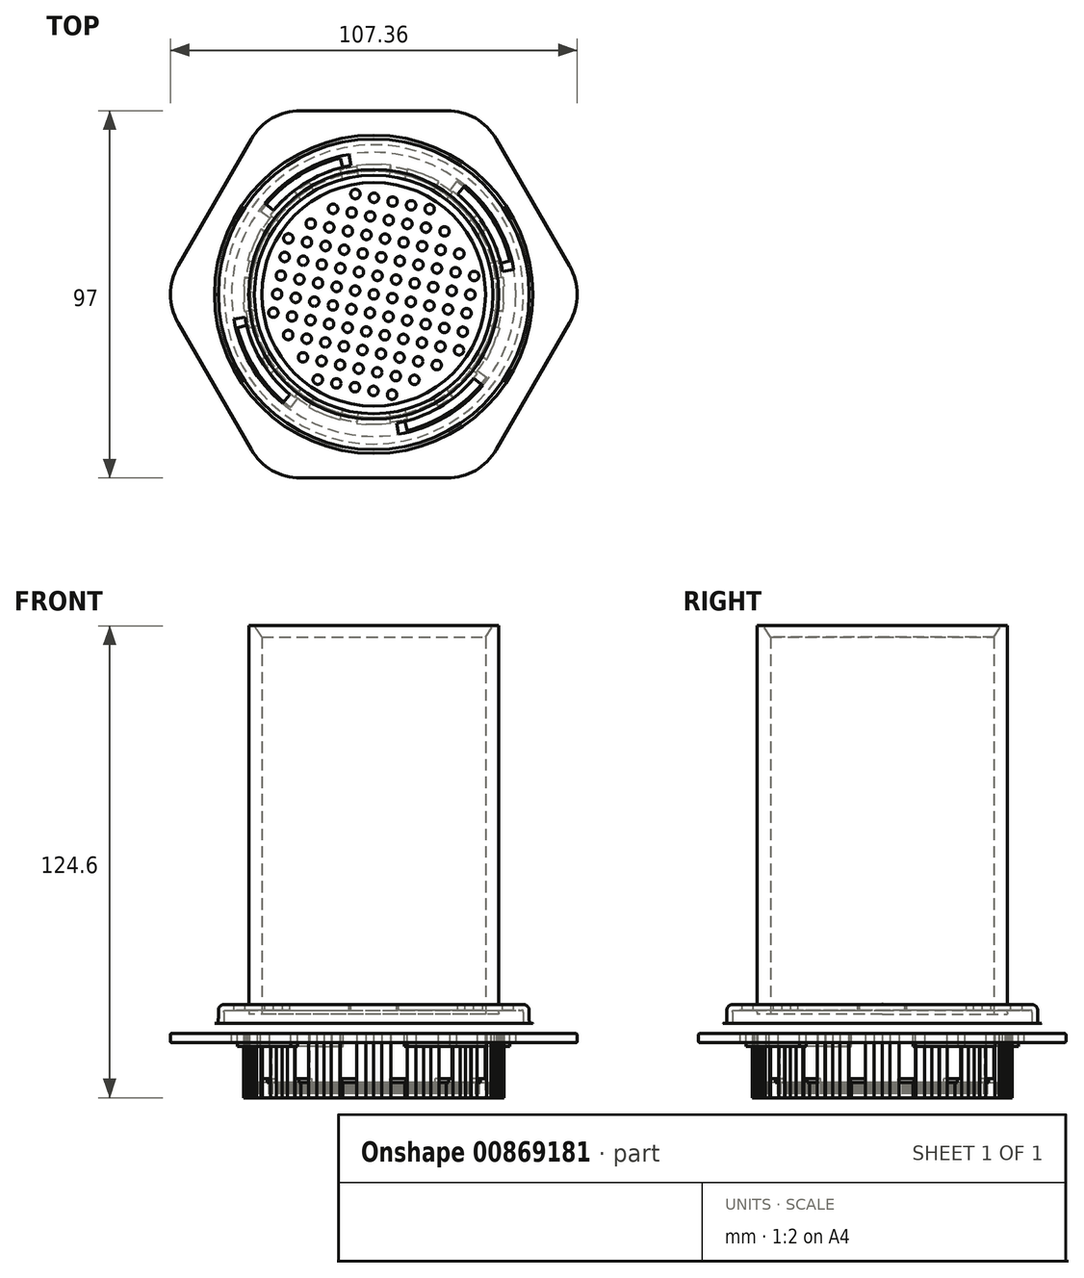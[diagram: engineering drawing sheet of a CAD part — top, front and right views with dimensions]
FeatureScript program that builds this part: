
annotation { "Feature Type Name" : "Feature", "Feature Type Description" : "" }
export const myFeature = defineFeature(function(context is Context, id is Id, definition is map)
    precondition{}
    {
        {
            var Q0;
            Q0=qCreatedBy(makeId("Top.planeOp"),FACE);
            var sketch = newSketch(context, id + "F0", { "sketchPlane" : qUnion([Q0])});
            skCircle(sketch, "E0.cCircle", {"center": v(0, 0) * mm, "radius": 48.5 * mm, "construction": true});
            skLineSegment(sketch, "E0.0", {"start": v(28, -48.5) * mm, "end": v(-28, -48.5) * mm});
            skLineSegment(sketch, "E0.1", {"start": v(-28, -48.5) * mm, "end": v(-56, 0) * mm});
            skLineSegment(sketch, "E0.2", {"start": v(-56, 0) * mm, "end": v(-28, 48.5) * mm});
            skLineSegment(sketch, "E0.3", {"start": v(-28, 48.5) * mm, "end": v(28, 48.5) * mm});
            skLineSegment(sketch, "E0.4", {"start": v(28, 48.5) * mm, "end": v(56, 0) * mm});
            skLineSegment(sketch, "E0.5", {"start": v(56, 0) * mm, "end": v(28, -48.5) * mm});
            skPoint(sketch, "E0.0.midPoint", {"position": v(0, -48.5) * mm});
            skCircle(sketch, "E1", {"center": v(0, 0) * mm, "radius": 42 * mm, "construction": true});
            skSolve(sketch);
        }
        {
            var Q0;
            Q0=makeQuery(id+"F0.imprint","IMPRINT",FACE,{"disambiguationData":[TD([[makeQuery(id+"F0.imprint","IMPRINT",EDGE,{"derivedFrom":sQuery(id+"F0.wireOp",EDGE,"E0.0")}),-1.0]])]});
            extrude(context, id + "F1", {"entities" : qUnion([Q0]), "oppositeDirection" : true, "depth" : 2.5 * mm, "offsetDistance" : 25 * mm});
        }
        {
            var Q0;
            Q0=makeQuery(id+"F1.opExtrude","CAP_EDGE",EDGE,{"disambiguationData":[OSD([sQuery(id+"F0.wireOp",EDGE,"E0.0")])],"isStart":false});
            var Q1;
            Q1=makeQuery(id+"F1.opExtrude","CAP_EDGE",EDGE,{"disambiguationData":[OSD([sQuery(id+"F0.wireOp",EDGE,"E0.5")])],"isStart":false});
            var Q2;
            Q2=makeQuery(id+"F1.opExtrude","CAP_EDGE",EDGE,{"disambiguationData":[OSD([sQuery(id+"F0.wireOp",EDGE,"E0.4")])],"isStart":false});
            var Q3;
            Q3=makeQuery(id+"F1.opExtrude","CAP_EDGE",EDGE,{"disambiguationData":[OSD([sQuery(id+"F0.wireOp",EDGE,"E0.3")])],"isStart":false});
            var Q4;
            Q4=makeQuery(id+"F1.opExtrude","CAP_EDGE",EDGE,{"disambiguationData":[OSD([sQuery(id+"F0.wireOp",EDGE,"E0.2")])],"isStart":false});
            var Q5;
            Q5=makeQuery(id+"F1.opExtrude","CAP_EDGE",EDGE,{"disambiguationData":[OSD([sQuery(id+"F0.wireOp",EDGE,"E0.1")])],"isStart":false});
            var Q6;
            Q6=makeQuery(id+"F1.opExtrude","CAP_FACE",FACE,{"disambiguationData":[OSD([sQuery(id+"F0.wireOp",EDGE,"E0.0"),sQuery(id+"F0.wireOp",EDGE,"E0.1"),sQuery(id+"F0.wireOp",EDGE,"E0.2"),sQuery(id+"F0.wireOp",EDGE,"E0.3"),sQuery(id+"F0.wireOp",EDGE,"E0.4"),sQuery(id+"F0.wireOp",EDGE,"E0.5")])],"isStart":true});
            fillet(context, id + "F2", {"entities" : qUnion([Q0, Q1, Q2, Q3, Q4, Q5, Q6]), "radius" : .5 * mm, "tangentPropagation" : true, "allowEdgeOverflow" : false});
        }
        {
            var Q0;
            Q0=makeQuery(id+"F1.opExtrude","SWEPT_EDGE",EDGE,{"disambiguationData":[OSD([sQuery(id+"F0.wireOp",EDGE,"E0.0"),sQuery(id+"F0.wireOp",EDGE,"E0.1")])]});
            var Q1;
            Q1=makeQuery(id+"F1.opExtrude","SWEPT_EDGE",EDGE,{"disambiguationData":[OSD([sQuery(id+"F0.wireOp",EDGE,"E0.0"),sQuery(id+"F0.wireOp",EDGE,"E0.5")])]});
            var Q2;
            Q2=makeQuery(id+"F1.opExtrude","SWEPT_EDGE",EDGE,{"disambiguationData":[OSD([sQuery(id+"F0.wireOp",EDGE,"E0.4"),sQuery(id+"F0.wireOp",EDGE,"E0.5")])]});
            var Q3;
            Q3=makeQuery(id+"F1.opExtrude","SWEPT_EDGE",EDGE,{"disambiguationData":[OSD([sQuery(id+"F0.wireOp",EDGE,"E0.3"),sQuery(id+"F0.wireOp",EDGE,"E0.4")])]});
            var Q4;
            Q4=makeQuery(id+"F1.opExtrude","SWEPT_EDGE",EDGE,{"disambiguationData":[OSD([sQuery(id+"F0.wireOp",EDGE,"E0.2"),sQuery(id+"F0.wireOp",EDGE,"E0.3")])]});
            var Q5;
            Q5=makeQuery(id+"F1.opExtrude","SWEPT_EDGE",EDGE,{"disambiguationData":[OSD([sQuery(id+"F0.wireOp",EDGE,"E0.1"),sQuery(id+"F0.wireOp",EDGE,"E0.2")])]});
            fillet(context, id + "F3", {"entities" : qUnion([Q0, Q1, Q2, Q3, Q4, Q5]), "radius" : 15 * mm, "tangentPropagation" : true, "allowEdgeOverflow" : false});
        }
        {
            var Q0;
            Q0=qCreatedBy(makeId("Right.planeOp"),FACE);
            var sketch = newSketch(context, id + "F4", { "sketchPlane" : qUnion([Q0])});
            skLineSegment(sketch, "E2", {"start": v(-39.5, 2.6) * mm, "end": v(-41, 2.6) * mm, "construction": true});
            skLineSegment(sketch, "E3", {"start": v(-39.5, 2.6) * mm, "end": v(-41, 2.6) * mm});
            skLineSegment(sketch, "E4", {"start": v(-41, 5.1) * mm, "end": v(-41, 7.6) * mm});
            skLineSegment(sketch, "E5", {"start": v(-41, 7.6) * mm, "end": v(-33.5, 7.6) * mm});
            skLineSegment(sketch, "E6", {"start": v(-33, 8.1) * mm, "end": v(-33, 107.6) * mm});
            skLineSegment(sketch, "E7", {"start": v(-33, 107.6) * mm, "end": v(-31.5, 107.6) * mm});
            skLineSegment(sketch, "E8", {"start": v(-29.5, 104.6) * mm, "end": v(-31.5, 107.6) * mm});
            skLineSegment(sketch, "E9", {"start": v(0, 0) * mm, "end": v(0, 27.78) * mm, "construction": true});
            skLineSegment(sketch, "E10", {"start": v(-41, 2.6) * mm, "end": v(-42, 2.6) * mm});
            skFitSpline(sketch, "E11", {"points": [v(-42, 2.6) * mm, v(-41, 5.1) * mm], "startDerivative": vector(3, 0) * mm, "endDerivative": vector(0, 7.5) * mm});
            skLineSegment(sketch, "E12", {"start": v(-29.5, -6.9) * mm, "end": v(-31, -6.9) * mm});
            skLineSegment(sketch, "E13", {"start": v(-31, -6.9) * mm, "end": v(-33, -3.9) * mm});
            skLineSegment(sketch, "E14", {"start": v(-29.5, 104.6) * mm, "end": v(-29.5, -6.9) * mm});
            skLineSegment(sketch, "E15", {"start": v(-33.5, 6.1) * mm, "end": v(-39, 6.1) * mm});
            skLineSegment(sketch, "E16", {"start": v(-39.5, 5.6) * mm, "end": v(-39.5, 2.6) * mm});
            skPoint(sketch, "E17.end.orphan", {"position": v(-33, 2.6) * mm});
            skLineSegment(sketch, "E18", {"start": v(-33, 5.6) * mm, "end": v(-33, -3.9) * mm});
            skFitSpline(sketch, "E19", {"points": [v(-33.5, 6.1) * mm, v(-33, 5.6) * mm], "startDerivative": vector(1.5, 0) * mm, "endDerivative": vector(0, -1.5) * mm});
            skFitSpline(sketch, "E20", {"points": [v(-39.5, 5.6) * mm, v(-39, 6.1) * mm], "startDerivative": vector(0, 1.5) * mm, "endDerivative": vector(1.5, 0) * mm});
            skFitSpline(sketch, "E21", {"points": [v(-33, 8.1) * mm, v(-33.5, 7.6) * mm], "startDerivative": vector(0, -1.5) * mm, "endDerivative": vector(-1.5, 0) * mm});
            skSolve(sketch);
        }
        {
            var Q0;
            Q0=makeQuery(id+"F4.imprint","IMPRINT",FACE,{"disambiguationData":[TD([[makeQuery(id+"F4.imprint","IMPRINT",EDGE,{"derivedFrom":sQuery(id+"F4.wireOp",EDGE,"E3")}),-1.0]])]});
            var Q1;
            Q1=sQuery(id+"F4.wireOp",EDGE,"E9");
            revolve(context, id + "F5", {"surfaceOperationType" : NewSurfaceOperationType.NEW, "entities" : qUnion([Q0]), "axis" : qUnion([Q1]), "revolveType" : RevolveType.FULL});
        }
        {
            var Q0;
            Q0=makeQuery(id+"F5.opRevolve","SWEPT_EDGE",EDGE,{"disambiguationData":[OSD([sQuery(id+"F4.wireOp",EDGE,"E4"),sQuery(id+"F4.wireOp",EDGE,"E5")])]});
            fillet(context, id + "F6", {"entities" : qUnion([Q0]), "radius" : 1.5 * mm, "tangentPropagation" : true, "allowEdgeOverflow" : false});
        }
        {
            var Q0;
            Q0=makeQuery(id+"F1.opExtrude","CAP_FACE",FACE,{"disambiguationData":[OSD([sQuery(id+"F0.wireOp",EDGE,"E0.0"),sQuery(id+"F0.wireOp",EDGE,"E0.1"),sQuery(id+"F0.wireOp",EDGE,"E0.2"),sQuery(id+"F0.wireOp",EDGE,"E0.3"),sQuery(id+"F0.wireOp",EDGE,"E0.4"),sQuery(id+"F0.wireOp",EDGE,"E0.5")])],"isStart":true});
            var sketch = newSketch(context, id + "F7", { "sketchPlane" : qUnion([Q0])});
            skArc(sketch, "E22", {"start": v(-6.51, 36.93) * mm, "mid": v(9.7, 36.22) * mm, "end": v(24.1, 28.73) * mm});
            skLineSegment(sketch, "E23", {"start": v(-6, 33.98) * mm, "end": v(-6.51, 36.93) * mm});
            skLineSegment(sketch, "E24", {"start": v(24.1, 28.73) * mm, "end": v(22.18, 26.43) * mm});
            skArc(sketch, "E25", {"start": v(22.18, 26.43) * mm, "mid": v(29.88, 17.25) * mm, "end": v(33.98, 6) * mm});
            skArc(sketch, "E26", {"start": v(36.93, 6.51) * mm, "mid": v(36.22, -9.7) * mm, "end": v(28.73, -24.1) * mm});
            skLineSegment(sketch, "E27", {"start": v(33.98, 6) * mm, "end": v(36.93, 6.51) * mm});
            skLineSegment(sketch, "E28", {"start": v(28.73, -24.1) * mm, "end": v(26.43, -22.18) * mm});
            skArc(sketch, "E29", {"start": v(26.43, -22.18) * mm, "mid": v(17.25, -29.88) * mm, "end": v(6, -33.98) * mm});
            skArc(sketch, "E30", {"start": v(6.51, -36.93) * mm, "mid": v(-9.7, -36.22) * mm, "end": v(-24.1, -28.73) * mm});
            skLineSegment(sketch, "E31", {"start": v(6, -33.98) * mm, "end": v(6.51, -36.93) * mm});
            skLineSegment(sketch, "E32", {"start": v(-24.1, -28.73) * mm, "end": v(-22.18, -26.43) * mm});
            skArc(sketch, "E33", {"start": v(-22.18, -26.43) * mm, "mid": v(-29.88, -17.25) * mm, "end": v(-33.98, -6) * mm});
            skArc(sketch, "E34", {"start": v(-36.93, -6.51) * mm, "mid": v(-36.22, 9.7) * mm, "end": v(-28.73, 24.1) * mm});
            skLineSegment(sketch, "E35", {"start": v(-33.98, -6) * mm, "end": v(-36.93, -6.51) * mm});
            skLineSegment(sketch, "E36", {"start": v(-28.73, 24.1) * mm, "end": v(-26.43, 22.18) * mm});
            skArc(sketch, "E37", {"start": v(-26.43, 22.18) * mm, "mid": v(-17.25, 29.88) * mm, "end": v(-6, 33.98) * mm});
            skLineSegment(sketch, "E38.0", {"start": v(-33.98, -6) * mm, "end": v(0, 0) * mm, "construction": true});
            skLineSegment(sketch, "E39.0", {"start": v(0, 0) * mm, "end": v(33.98, 6) * mm, "construction": true});
            skLineSegment(sketch, "E40.0", {"start": v(6.51, -36.93) * mm, "end": v(0, 0) * mm, "construction": true});
            skLineSegment(sketch, "E41.0", {"start": v(0, 0) * mm, "end": v(-6.51, 36.93) * mm, "construction": true});
            skSolve(sketch);
        }
        {
            var Q0;
            Q0 = qSketchRegion(id + "F7", true);
            extrude(context, id + "F8", {"entities" : qUnion([Q0]), "operationType" : NewBodyOperationType.REMOVE, "oppositeDirection" : true, "depth" : 10 * mm, "offsetDistance" : 25 * mm, "symmetric" : true});
        }
        {
            var Q0;
            Q0=makeQuery(id+"F5.opRevolve","SWEPT_FACE",FACE,{"disambiguationData":[OSD([sQuery(id+"F4.wireOp",EDGE,"E5")])]});
            var sketch = newSketch(context, id + "F9", { "sketchPlane" : qUnion([Q0])});
            skLineSegment(sketch, "E42", {"start": v(22.18, 26.43) * mm, "end": v(24.1, 28.73) * mm});
            skLineSegment(sketch, "E43.3.2", {"start": v(33.98, 6) * mm, "end": v(36.93, 6.51) * mm});
            skPoint(sketch, "E43.center", {"position": v(0, 0) * mm});
            skArc(sketch, "E44", {"start": v(24.1, 28.73) * mm, "mid": v(32.48, 18.75) * mm, "end": v(36.93, 6.51) * mm});
            skArc(sketch, "E45", {"start": v(22.18, 26.43) * mm, "mid": v(29.88, 17.25) * mm, "end": v(33.98, 6) * mm});
            skArc(sketch, "E46.1.0", {"start": v(-28.73, 24.1) * mm, "mid": v(-18.75, 32.48) * mm, "end": v(-6.51, 36.93) * mm});
            skLineSegment(sketch, "E46.1.1", {"start": v(-6, 33.98) * mm, "end": v(-6.51, 36.93) * mm});
            skLineSegment(sketch, "E46.1.2", {"start": v(-26.43, 22.18) * mm, "end": v(-28.73, 24.1) * mm});
            skArc(sketch, "E46.1.3", {"start": v(-26.43, 22.18) * mm, "mid": v(-17.25, 29.88) * mm, "end": v(-6, 33.98) * mm});
            skArc(sketch, "E46.2.0", {"start": v(-24.1, -28.73) * mm, "mid": v(-32.48, -18.75) * mm, "end": v(-36.93, -6.51) * mm});
            skLineSegment(sketch, "E46.2.1", {"start": v(-33.98, -6) * mm, "end": v(-36.93, -6.51) * mm});
            skLineSegment(sketch, "E46.2.2", {"start": v(-22.18, -26.43) * mm, "end": v(-24.1, -28.73) * mm});
            skArc(sketch, "E46.2.3", {"start": v(-22.18, -26.43) * mm, "mid": v(-29.88, -17.25) * mm, "end": v(-33.98, -6) * mm});
            skArc(sketch, "E46.3.0", {"start": v(28.73, -24.1) * mm, "mid": v(18.75, -32.48) * mm, "end": v(6.51, -36.93) * mm});
            skLineSegment(sketch, "E46.3.1", {"start": v(6, -33.98) * mm, "end": v(6.51, -36.93) * mm});
            skLineSegment(sketch, "E46.3.2", {"start": v(26.43, -22.18) * mm, "end": v(28.73, -24.1) * mm});
            skArc(sketch, "E46.3.3", {"start": v(26.43, -22.18) * mm, "mid": v(17.25, -29.88) * mm, "end": v(6, -33.98) * mm});
            skSolve(sketch);
        }
        {
            var Q0;
            Q0 = qSketchRegion(id + "F9", true);
            extrude(context, id + "F10", {"entities" : qUnion([Q0]), "operationType" : NewBodyOperationType.REMOVE, "oppositeDirection" : true, "depth" : 10 * mm, "offsetDistance" : 25 * mm});
        }
        {
            var Q0;
            Q0=qCreatedBy(makeId("Top.planeOp"),FACE);
            var sketch = newSketch(context, id + "F11", { "sketchPlane" : qUnion([Q0])});
            skCircle(sketch, "E47", {"center": v(0, 0) * mm, "radius": 34 * mm});
            skSolve(sketch);
        }
        {
            var Q0;
            Q0 = qSketchRegion(id + "F11", true);
            extrude(context, id + "F12", {"entities" : qUnion([Q0]), "oppositeDirection" : true, "depth" : 17 * mm, "offsetDistance" : 25 * mm});
        }
        {
            var Q0;
            Q0=makeQuery(id+"F12.opExtrude","CAP_FACE",FACE,{"disambiguationData":[OSD([sQuery(id+"F11.wireOp",EDGE,"E47")])],"isStart":true});
            var sketch = newSketch(context, id + "F13", { "sketchPlane" : qUnion([Q0])});
            skCircle(sketch, "E48", {"center": v(0, 0) * mm, "radius": 32.5 * mm});
            skSolve(sketch);
        }
        {
            var Q0;
            Q0 = qSketchRegion(id + "F13", true);
            extrude(context, id + "F14", {"entities" : qUnion([Q0]), "operationType" : NewBodyOperationType.REMOVE, "oppositeDirection" : true, "depth" : 13 * mm, "offsetDistance" : 25 * mm});
        }
        {
            var Q0;
            Q0=makeQuery(id+"F12.opExtrude","CAP_FACE",FACE,{"disambiguationData":[OSD([sQuery(id+"F11.wireOp",EDGE,"E47")])],"isStart":true});
            var sketch = newSketch(context, id + "F15", { "sketchPlane" : qUnion([Q0])});
            skLineSegment(sketch, "E49", {"start": v(0, 0) * mm, "end": v(0, 19.24) * mm, "construction": true});
            skLineSegment(sketch, "E50", {"start": v(0, 0) * mm, "end": v(-8.08, 33.03) * mm, "construction": true});
            skLineSegment(sketch, "E51", {"start": v(0, 0) * mm, "end": v(-8.8, 35.94) * mm, "construction": true});
            skLineSegment(sketch, "E52", {"start": v(0, 0) * mm, "end": v(-29.84, 21.88) * mm, "construction": true});
            skArc(sketch, "E53", {"start": v(-29.84, 21.88) * mm, "mid": v(-20.56, 30.76) * mm, "end": v(-8.8, 35.94) * mm});
            skArc(sketch, "E54", {"start": v(-27.42, 20.1) * mm, "mid": v(-18.89, 28.27) * mm, "end": v(-8.08, 33.03) * mm});
            skLineSegment(sketch, "E55", {"start": v(-27.42, 20.1) * mm, "end": v(-29.84, 21.88) * mm});
            skLineSegment(sketch, "E56", {"start": v(-8.8, 35.94) * mm, "end": v(-8.08, 33.03) * mm});
            skArc(sketch, "E57.1.0", {"start": v(-20.1, -27.42) * mm, "mid": v(-28.27, -18.89) * mm, "end": v(-33.03, -8.08) * mm});
            skArc(sketch, "E57.1.1", {"start": v(-21.88, -29.84) * mm, "mid": v(-30.76, -20.56) * mm, "end": v(-35.94, -8.8) * mm});
            skLineSegment(sketch, "E57.1.2", {"start": v(-20.1, -27.42) * mm, "end": v(-21.88, -29.84) * mm});
            skLineSegment(sketch, "E57.1.3", {"start": v(-35.94, -8.8) * mm, "end": v(-33.03, -8.08) * mm});
            skArc(sketch, "E57.2.0", {"start": v(27.42, -20.1) * mm, "mid": v(18.89, -28.27) * mm, "end": v(8.08, -33.03) * mm});
            skArc(sketch, "E57.2.1", {"start": v(29.84, -21.88) * mm, "mid": v(20.56, -30.76) * mm, "end": v(8.8, -35.94) * mm});
            skLineSegment(sketch, "E57.2.2", {"start": v(27.42, -20.1) * mm, "end": v(29.84, -21.88) * mm});
            skLineSegment(sketch, "E57.2.3", {"start": v(8.8, -35.94) * mm, "end": v(8.08, -33.03) * mm});
            skArc(sketch, "E57.3.0", {"start": v(20.1, 27.42) * mm, "mid": v(28.27, 18.89) * mm, "end": v(33.03, 8.08) * mm});
            skArc(sketch, "E57.3.1", {"start": v(21.88, 29.84) * mm, "mid": v(30.76, 20.56) * mm, "end": v(35.94, 8.8) * mm});
            skLineSegment(sketch, "E57.3.2", {"start": v(20.1, 27.42) * mm, "end": v(21.88, 29.84) * mm});
            skLineSegment(sketch, "E57.3.3", {"start": v(35.94, 8.8) * mm, "end": v(33.03, 8.08) * mm});
            skSolve(sketch);
        }
        {
            var Q0;
            Q0 = qSketchRegion(id + "F15", true);
            extrude(context, id + "F16", {"entities" : qUnion([Q0]), "operationType" : NewBodyOperationType.ADD, "oppositeDirection" : true, "depth" : 3.5 * mm, "offsetDistance" : 25 * mm});
        }
        {
            var Q0;
            Q0=makeQuery(id+"F12.opExtrude","CAP_FACE",FACE,{"disambiguationData":[OSD([sQuery(id+"F11.wireOp",EDGE,"E47")])],"isStart":false});
            var sketch = newSketch(context, id + "F17", { "sketchPlane" : qUnion([Q0])});
            skLineSegment(sketch, "E58", {"start": v(6.96, 52.9) * mm, "end": v(6.96, 53.63) * mm, "construction": true});
            skLineSegment(sketch, "E59", {"start": v(-4.49, 34.08) * mm, "end": v(-2.1, 34.31) * mm});
            skLineSegment(sketch, "E60", {"start": v(-2.1, 34.19) * mm, "end": v(0, 34.25) * mm});
            skLineSegment(sketch, "E61", {"start": v(0, 34.25) * mm, "end": v(2.1, 34.19) * mm});
            skLineSegment(sketch, "E62", {"start": v(-2.1, 34.31) * mm, "end": v(-2.1, 34.19) * mm});
            skLineSegment(sketch, "E63", {"start": v(-4.43, 33.68) * mm, "end": v(-4.49, 34.08) * mm});
            skLineSegment(sketch, "E64", {"start": v(2.1, 34.19) * mm, "end": v(2.1, 34.31) * mm});
            skLineSegment(sketch, "E65", {"start": v(4.49, 34.08) * mm, "end": v(2.1, 34.31) * mm});
            skLineSegment(sketch, "E66", {"start": v(4.49, 34.08) * mm, "end": v(4.44, 33.7) * mm});
            skArc(sketch, "E67", {"start": v(-4.43, 33.68) * mm, "mid": v(0, 33.97) * mm, "end": v(4.43, 33.68) * mm});
            skArc(sketch, "E68.1.0", {"start": v(-16.99, 29.42) * mm, "mid": v(-13, 31.38) * mm, "end": v(-8.8, 32.81) * mm});
            skLineSegment(sketch, "E68.1.1", {"start": v(-13.1, 31.64) * mm, "end": v(-11.15, 32.38) * mm});
            skLineSegment(sketch, "E68.1.2", {"start": v(-17.19, 29.77) * mm, "end": v(-15.07, 30.9) * mm});
            skLineSegment(sketch, "E68.1.3", {"start": v(-15.01, 30.78) * mm, "end": v(-13.1, 31.64) * mm});
            skLineSegment(sketch, "E68.1.4", {"start": v(-8.9, 33.2) * mm, "end": v(-11.2, 32.5) * mm});
            skLineSegment(sketch, "E68.1.5", {"start": v(-16.99, 29.42) * mm, "end": v(-17.19, 29.77) * mm});
            skLineSegment(sketch, "E68.1.6", {"start": v(-8.9, 33.2) * mm, "end": v(-8.8, 32.84) * mm});
            skLineSegment(sketch, "E68.1.7", {"start": v(-11.15, 32.38) * mm, "end": v(-11.2, 32.5) * mm});
            skLineSegment(sketch, "E68.1.8", {"start": v(-15.07, 30.9) * mm, "end": v(-15.01, 30.78) * mm});
            skArc(sketch, "E68.2.0", {"start": v(-26.95, 20.68) * mm, "mid": v(-24.02, 24.02) * mm, "end": v(-20.68, 26.95) * mm});
            skLineSegment(sketch, "E68.2.1", {"start": v(-24.22, 24.22) * mm, "end": v(-22.7, 25.65) * mm});
            skLineSegment(sketch, "E68.2.2", {"start": v(-27.27, 20.93) * mm, "end": v(-25.75, 22.78) * mm});
            skLineSegment(sketch, "E68.2.3", {"start": v(-25.65, 22.7) * mm, "end": v(-24.22, 24.22) * mm});
            skLineSegment(sketch, "E68.2.4", {"start": v(-20.93, 27.27) * mm, "end": v(-22.78, 25.75) * mm});
            skLineSegment(sketch, "E68.2.5", {"start": v(-26.95, 20.68) * mm, "end": v(-27.27, 20.93) * mm});
            skLineSegment(sketch, "E68.2.6", {"start": v(-20.93, 27.27) * mm, "end": v(-20.7, 26.98) * mm});
            skLineSegment(sketch, "E68.2.7", {"start": v(-22.7, 25.65) * mm, "end": v(-22.78, 25.75) * mm});
            skLineSegment(sketch, "E68.2.8", {"start": v(-25.75, 22.78) * mm, "end": v(-25.65, 22.7) * mm});
            skArc(sketch, "E68.3.0", {"start": v(-32.81, 8.8) * mm, "mid": v(-31.38, 13) * mm, "end": v(-29.42, 16.99) * mm});
            skLineSegment(sketch, "E68.3.1", {"start": v(-31.64, 13.1) * mm, "end": v(-30.78, 15.01) * mm});
            skLineSegment(sketch, "E68.3.2", {"start": v(-33.2, 8.9) * mm, "end": v(-32.5, 11.2) * mm});
            skLineSegment(sketch, "E68.3.3", {"start": v(-32.38, 11.15) * mm, "end": v(-31.64, 13.1) * mm});
            skLineSegment(sketch, "E68.3.4", {"start": v(-29.77, 17.19) * mm, "end": v(-30.9, 15.07) * mm});
            skLineSegment(sketch, "E68.3.5", {"start": v(-32.81, 8.8) * mm, "end": v(-33.2, 8.9) * mm});
            skLineSegment(sketch, "E68.3.6", {"start": v(-29.77, 17.19) * mm, "end": v(-29.44, 17) * mm});
            skLineSegment(sketch, "E68.3.7", {"start": v(-30.78, 15.01) * mm, "end": v(-30.9, 15.07) * mm});
            skLineSegment(sketch, "E68.3.8", {"start": v(-32.5, 11.2) * mm, "end": v(-32.38, 11.15) * mm});
            skArc(sketch, "E68.4.0", {"start": v(-33.68, -4.43) * mm, "mid": v(-33.97, 0) * mm, "end": v(-33.68, 4.43) * mm});
            skLineSegment(sketch, "E68.4.1", {"start": v(-34.25, 0) * mm, "end": v(-34.19, 2.1) * mm});
            skLineSegment(sketch, "E68.4.2", {"start": v(-34.08, -4.49) * mm, "end": v(-34.31, -2.1) * mm});
            skLineSegment(sketch, "E68.4.3", {"start": v(-34.19, -2.1) * mm, "end": v(-34.25, 0) * mm});
            skLineSegment(sketch, "E68.4.4", {"start": v(-34.08, 4.49) * mm, "end": v(-34.31, 2.1) * mm});
            skLineSegment(sketch, "E68.4.5", {"start": v(-33.68, -4.43) * mm, "end": v(-34.08, -4.49) * mm});
            skLineSegment(sketch, "E68.4.6", {"start": v(-34.08, 4.49) * mm, "end": v(-33.7, 4.44) * mm});
            skLineSegment(sketch, "E68.4.7", {"start": v(-34.19, 2.1) * mm, "end": v(-34.31, 2.1) * mm});
            skLineSegment(sketch, "E68.4.8", {"start": v(-34.31, -2.1) * mm, "end": v(-34.19, -2.1) * mm});
            skArc(sketch, "E68.5.0", {"start": v(-29.42, -16.99) * mm, "mid": v(-31.38, -13) * mm, "end": v(-32.81, -8.8) * mm});
            skLineSegment(sketch, "E68.5.1", {"start": v(-31.64, -13.1) * mm, "end": v(-32.38, -11.15) * mm});
            skLineSegment(sketch, "E68.5.2", {"start": v(-29.77, -17.19) * mm, "end": v(-30.9, -15.07) * mm});
            skLineSegment(sketch, "E68.5.3", {"start": v(-30.78, -15.01) * mm, "end": v(-31.64, -13.1) * mm});
            skLineSegment(sketch, "E68.5.4", {"start": v(-33.2, -8.9) * mm, "end": v(-32.5, -11.2) * mm});
            skLineSegment(sketch, "E68.5.5", {"start": v(-29.42, -16.99) * mm, "end": v(-29.77, -17.19) * mm});
            skLineSegment(sketch, "E68.5.6", {"start": v(-33.2, -8.9) * mm, "end": v(-32.84, -8.8) * mm});
            skLineSegment(sketch, "E68.5.7", {"start": v(-32.38, -11.15) * mm, "end": v(-32.5, -11.2) * mm});
            skLineSegment(sketch, "E68.5.8", {"start": v(-30.9, -15.07) * mm, "end": v(-30.78, -15.01) * mm});
            skArc(sketch, "E68.6.0", {"start": v(-20.68, -26.95) * mm, "mid": v(-24.02, -24.02) * mm, "end": v(-26.95, -20.68) * mm});
            skLineSegment(sketch, "E68.6.1", {"start": v(-24.22, -24.22) * mm, "end": v(-25.65, -22.7) * mm});
            skLineSegment(sketch, "E68.6.2", {"start": v(-20.93, -27.27) * mm, "end": v(-22.78, -25.75) * mm});
            skLineSegment(sketch, "E68.6.3", {"start": v(-22.7, -25.65) * mm, "end": v(-24.22, -24.22) * mm});
            skLineSegment(sketch, "E68.6.4", {"start": v(-27.27, -20.93) * mm, "end": v(-25.75, -22.78) * mm});
            skLineSegment(sketch, "E68.6.5", {"start": v(-20.68, -26.95) * mm, "end": v(-20.93, -27.27) * mm});
            skLineSegment(sketch, "E68.6.6", {"start": v(-27.27, -20.93) * mm, "end": v(-26.98, -20.7) * mm});
            skLineSegment(sketch, "E68.6.7", {"start": v(-25.65, -22.7) * mm, "end": v(-25.75, -22.78) * mm});
            skLineSegment(sketch, "E68.6.8", {"start": v(-22.78, -25.75) * mm, "end": v(-22.7, -25.65) * mm});
            skArc(sketch, "E68.7.0", {"start": v(-8.8, -32.81) * mm, "mid": v(-13, -31.38) * mm, "end": v(-16.99, -29.42) * mm});
            skLineSegment(sketch, "E68.7.1", {"start": v(-13.1, -31.64) * mm, "end": v(-15.01, -30.78) * mm});
            skLineSegment(sketch, "E68.7.2", {"start": v(-8.9, -33.2) * mm, "end": v(-11.2, -32.5) * mm});
            skLineSegment(sketch, "E68.7.3", {"start": v(-11.15, -32.38) * mm, "end": v(-13.1, -31.64) * mm});
            skLineSegment(sketch, "E68.7.4", {"start": v(-17.19, -29.77) * mm, "end": v(-15.07, -30.9) * mm});
            skLineSegment(sketch, "E68.7.5", {"start": v(-8.8, -32.81) * mm, "end": v(-8.9, -33.2) * mm});
            skLineSegment(sketch, "E68.7.6", {"start": v(-17.19, -29.77) * mm, "end": v(-17, -29.44) * mm});
            skLineSegment(sketch, "E68.7.7", {"start": v(-15.01, -30.78) * mm, "end": v(-15.07, -30.9) * mm});
            skLineSegment(sketch, "E68.7.8", {"start": v(-11.2, -32.5) * mm, "end": v(-11.15, -32.38) * mm});
            skArc(sketch, "E68.8.0", {"start": v(4.43, -33.68) * mm, "mid": v(0, -33.97) * mm, "end": v(-4.43, -33.68) * mm});
            skLineSegment(sketch, "E68.8.1", {"start": v(0, -34.25) * mm, "end": v(-2.1, -34.19) * mm});
            skLineSegment(sketch, "E68.8.2", {"start": v(4.49, -34.08) * mm, "end": v(2.1, -34.31) * mm});
            skLineSegment(sketch, "E68.8.3", {"start": v(2.1, -34.19) * mm, "end": v(0, -34.25) * mm});
            skLineSegment(sketch, "E68.8.4", {"start": v(-4.49, -34.08) * mm, "end": v(-2.1, -34.31) * mm});
            skLineSegment(sketch, "E68.8.5", {"start": v(4.43, -33.68) * mm, "end": v(4.49, -34.08) * mm});
            skLineSegment(sketch, "E68.8.6", {"start": v(-4.49, -34.08) * mm, "end": v(-4.44, -33.7) * mm});
            skLineSegment(sketch, "E68.8.7", {"start": v(-2.1, -34.19) * mm, "end": v(-2.1, -34.31) * mm});
            skLineSegment(sketch, "E68.8.8", {"start": v(2.1, -34.31) * mm, "end": v(2.1, -34.19) * mm});
            skArc(sketch, "E68.9.0", {"start": v(16.99, -29.42) * mm, "mid": v(13, -31.38) * mm, "end": v(8.8, -32.81) * mm});
            skLineSegment(sketch, "E68.9.1", {"start": v(13.1, -31.64) * mm, "end": v(11.15, -32.38) * mm});
            skLineSegment(sketch, "E68.9.2", {"start": v(17.19, -29.77) * mm, "end": v(15.07, -30.9) * mm});
            skLineSegment(sketch, "E68.9.3", {"start": v(15.01, -30.78) * mm, "end": v(13.1, -31.64) * mm});
            skLineSegment(sketch, "E68.9.4", {"start": v(8.9, -33.2) * mm, "end": v(11.2, -32.5) * mm});
            skLineSegment(sketch, "E68.9.5", {"start": v(16.99, -29.42) * mm, "end": v(17.19, -29.77) * mm});
            skLineSegment(sketch, "E68.9.6", {"start": v(8.9, -33.2) * mm, "end": v(8.8, -32.84) * mm});
            skLineSegment(sketch, "E68.9.7", {"start": v(11.15, -32.38) * mm, "end": v(11.2, -32.5) * mm});
            skLineSegment(sketch, "E68.9.8", {"start": v(15.07, -30.9) * mm, "end": v(15.01, -30.78) * mm});
            skArc(sketch, "E68.10.0", {"start": v(26.95, -20.68) * mm, "mid": v(24.02, -24.02) * mm, "end": v(20.68, -26.95) * mm});
            skLineSegment(sketch, "E68.10.1", {"start": v(24.22, -24.22) * mm, "end": v(22.7, -25.65) * mm});
            skLineSegment(sketch, "E68.10.2", {"start": v(27.27, -20.93) * mm, "end": v(25.75, -22.78) * mm});
            skLineSegment(sketch, "E68.10.3", {"start": v(25.65, -22.7) * mm, "end": v(24.22, -24.22) * mm});
            skLineSegment(sketch, "E68.10.4", {"start": v(20.93, -27.27) * mm, "end": v(22.78, -25.75) * mm});
            skLineSegment(sketch, "E68.10.5", {"start": v(26.95, -20.68) * mm, "end": v(27.27, -20.93) * mm});
            skLineSegment(sketch, "E68.10.6", {"start": v(20.93, -27.27) * mm, "end": v(20.7, -26.98) * mm});
            skLineSegment(sketch, "E68.10.7", {"start": v(22.7, -25.65) * mm, "end": v(22.78, -25.75) * mm});
            skLineSegment(sketch, "E68.10.8", {"start": v(25.75, -22.78) * mm, "end": v(25.65, -22.7) * mm});
            skArc(sketch, "E68.11.0", {"start": v(32.81, -8.8) * mm, "mid": v(31.38, -13) * mm, "end": v(29.42, -16.99) * mm});
            skLineSegment(sketch, "E68.11.1", {"start": v(31.64, -13.1) * mm, "end": v(30.78, -15.01) * mm});
            skLineSegment(sketch, "E68.11.2", {"start": v(33.2, -8.9) * mm, "end": v(32.5, -11.2) * mm});
            skLineSegment(sketch, "E68.11.3", {"start": v(32.38, -11.15) * mm, "end": v(31.64, -13.1) * mm});
            skLineSegment(sketch, "E68.11.4", {"start": v(29.77, -17.19) * mm, "end": v(30.9, -15.07) * mm});
            skLineSegment(sketch, "E68.11.5", {"start": v(32.81, -8.8) * mm, "end": v(33.2, -8.9) * mm});
            skLineSegment(sketch, "E68.11.6", {"start": v(29.77, -17.19) * mm, "end": v(29.44, -17) * mm});
            skLineSegment(sketch, "E68.11.7", {"start": v(30.78, -15.01) * mm, "end": v(30.9, -15.07) * mm});
            skLineSegment(sketch, "E68.11.8", {"start": v(32.5, -11.2) * mm, "end": v(32.38, -11.15) * mm});
            skArc(sketch, "E68.12.0", {"start": v(33.68, 4.43) * mm, "mid": v(33.97, 0) * mm, "end": v(33.68, -4.43) * mm});
            skLineSegment(sketch, "E68.12.1", {"start": v(34.25, 0) * mm, "end": v(34.19, -2.1) * mm});
            skLineSegment(sketch, "E68.12.2", {"start": v(34.08, 4.49) * mm, "end": v(34.31, 2.1) * mm});
            skLineSegment(sketch, "E68.12.3", {"start": v(34.19, 2.1) * mm, "end": v(34.25, 0) * mm});
            skLineSegment(sketch, "E68.12.4", {"start": v(34.08, -4.49) * mm, "end": v(34.31, -2.1) * mm});
            skLineSegment(sketch, "E68.12.5", {"start": v(33.68, 4.43) * mm, "end": v(34.08, 4.49) * mm});
            skLineSegment(sketch, "E68.12.6", {"start": v(34.08, -4.49) * mm, "end": v(33.7, -4.44) * mm});
            skLineSegment(sketch, "E68.12.7", {"start": v(34.19, -2.1) * mm, "end": v(34.31, -2.1) * mm});
            skLineSegment(sketch, "E68.12.8", {"start": v(34.31, 2.1) * mm, "end": v(34.19, 2.1) * mm});
            skArc(sketch, "E68.13.0", {"start": v(29.42, 16.99) * mm, "mid": v(31.38, 13) * mm, "end": v(32.81, 8.8) * mm});
            skLineSegment(sketch, "E68.13.1", {"start": v(31.64, 13.1) * mm, "end": v(32.38, 11.15) * mm});
            skLineSegment(sketch, "E68.13.2", {"start": v(29.77, 17.19) * mm, "end": v(30.9, 15.07) * mm});
            skLineSegment(sketch, "E68.13.3", {"start": v(30.78, 15.01) * mm, "end": v(31.64, 13.1) * mm});
            skLineSegment(sketch, "E68.13.4", {"start": v(33.2, 8.9) * mm, "end": v(32.5, 11.2) * mm});
            skLineSegment(sketch, "E68.13.5", {"start": v(29.42, 16.99) * mm, "end": v(29.77, 17.19) * mm});
            skLineSegment(sketch, "E68.13.6", {"start": v(33.2, 8.9) * mm, "end": v(32.84, 8.8) * mm});
            skLineSegment(sketch, "E68.13.7", {"start": v(32.38, 11.15) * mm, "end": v(32.5, 11.2) * mm});
            skLineSegment(sketch, "E68.13.8", {"start": v(30.9, 15.07) * mm, "end": v(30.78, 15.01) * mm});
            skArc(sketch, "E68.14.0", {"start": v(20.68, 26.95) * mm, "mid": v(24.02, 24.02) * mm, "end": v(26.95, 20.68) * mm});
            skLineSegment(sketch, "E68.14.1", {"start": v(24.22, 24.22) * mm, "end": v(25.65, 22.7) * mm});
            skLineSegment(sketch, "E68.14.2", {"start": v(20.93, 27.27) * mm, "end": v(22.78, 25.75) * mm});
            skLineSegment(sketch, "E68.14.3", {"start": v(22.7, 25.65) * mm, "end": v(24.22, 24.22) * mm});
            skLineSegment(sketch, "E68.14.4", {"start": v(27.27, 20.93) * mm, "end": v(25.75, 22.78) * mm});
            skLineSegment(sketch, "E68.14.5", {"start": v(20.68, 26.95) * mm, "end": v(20.93, 27.27) * mm});
            skLineSegment(sketch, "E68.14.6", {"start": v(27.27, 20.93) * mm, "end": v(26.98, 20.7) * mm});
            skLineSegment(sketch, "E68.14.7", {"start": v(25.65, 22.7) * mm, "end": v(25.75, 22.78) * mm});
            skLineSegment(sketch, "E68.14.8", {"start": v(22.78, 25.75) * mm, "end": v(22.7, 25.65) * mm});
            skArc(sketch, "E68.15.0", {"start": v(8.8, 32.81) * mm, "mid": v(13, 31.38) * mm, "end": v(16.99, 29.42) * mm});
            skLineSegment(sketch, "E68.15.1", {"start": v(13.1, 31.64) * mm, "end": v(15.01, 30.78) * mm});
            skLineSegment(sketch, "E68.15.2", {"start": v(8.9, 33.2) * mm, "end": v(11.2, 32.5) * mm});
            skLineSegment(sketch, "E68.15.3", {"start": v(11.15, 32.38) * mm, "end": v(13.1, 31.64) * mm});
            skLineSegment(sketch, "E68.15.4", {"start": v(17.19, 29.77) * mm, "end": v(15.07, 30.9) * mm});
            skLineSegment(sketch, "E68.15.5", {"start": v(8.8, 32.81) * mm, "end": v(8.9, 33.2) * mm});
            skLineSegment(sketch, "E68.15.6", {"start": v(17.19, 29.77) * mm, "end": v(17, 29.44) * mm});
            skLineSegment(sketch, "E68.15.7", {"start": v(15.01, 30.78) * mm, "end": v(15.07, 30.9) * mm});
            skLineSegment(sketch, "E68.15.8", {"start": v(11.2, 32.5) * mm, "end": v(11.15, 32.38) * mm});
            skSolve(sketch);
        }
        {
            var Q0;
            Q0 = qSketchRegion(id + "F17", true);
            var Q1;
            Q1=makeQuery(id+"F17.imprint","IMPRINT",FACE,{"disambiguationData":[TD([[makeQuery(id+"F17.imprint","IMPRINT",EDGE,{"derivedFrom":sQuery(id+"F17.wireOp",EDGE,"E68.2.1")}),-1.0]])]});
            var Q2;
            Q2=makeQuery(id+"F17.imprint","IMPRINT",FACE,{"disambiguationData":[TD([[makeQuery(id+"F17.imprint","IMPRINT",EDGE,{"derivedFrom":sQuery(id+"F17.wireOp",EDGE,"E68.3.1")}),-1.0]])]});
            var Q3;
            Q3=makeQuery(id+"F17.imprint","IMPRINT",FACE,{"disambiguationData":[TD([[makeQuery(id+"F17.imprint","IMPRINT",EDGE,{"derivedFrom":sQuery(id+"F17.wireOp",EDGE,"E68.12.1")}),-1.0]])]});
            var Q4;
            Q4=makeQuery(id+"F17.imprint","IMPRINT",FACE,{"disambiguationData":[TD([[makeQuery(id+"F17.imprint","IMPRINT",EDGE,{"derivedFrom":sQuery(id+"F17.wireOp",EDGE,"E68.5.1")}),-1.0]])]});
            var Q5;
            {var subQ4=sQuery(id+"F17.wireOp",EDGE,"E59");Q5=makeQuery(id+"F17.imprint","IMPRINT",FACE,{"disambiguationData":[TD([[makeQuery(id+"F17.imprint","IMPRINT",EDGE,{"derivedFrom":subQ4}),-1.0]])]});}
            var Q6;
            Q6=makeQuery(id+"F17.imprint","IMPRINT",FACE,{"disambiguationData":[TD([[makeQuery(id+"F17.imprint","IMPRINT",EDGE,{"derivedFrom":sQuery(id+"F17.wireOp",EDGE,"E68.6.1")}),-1.0]])]});
            var Q7;
            Q7=makeQuery(id+"F17.imprint","IMPRINT",FACE,{"disambiguationData":[TD([[makeQuery(id+"F17.imprint","IMPRINT",EDGE,{"derivedFrom":sQuery(id+"F17.wireOp",EDGE,"E68.13.1")}),-1.0]])]});
            var Q8;
            Q8=makeQuery(id+"F17.imprint","IMPRINT",FACE,{"disambiguationData":[TD([[makeQuery(id+"F17.imprint","IMPRINT",EDGE,{"derivedFrom":sQuery(id+"F17.wireOp",EDGE,"E68.10.1")}),-1.0]])]});
            var Q9;
            Q9=makeQuery(id+"F17.imprint","IMPRINT",FACE,{"disambiguationData":[TD([[makeQuery(id+"F17.imprint","IMPRINT",EDGE,{"derivedFrom":sQuery(id+"F17.wireOp",EDGE,"E68.1.1")}),-1.0]])]});
            var Q10;
            Q10=makeQuery(id+"F17.imprint","IMPRINT",FACE,{"disambiguationData":[TD([[makeQuery(id+"F17.imprint","IMPRINT",EDGE,{"derivedFrom":sQuery(id+"F17.wireOp",EDGE,"E68.8.1")}),-1.0]])]});
            var Q11;
            Q11=makeQuery(id+"F17.imprint","IMPRINT",FACE,{"disambiguationData":[TD([[makeQuery(id+"F17.imprint","IMPRINT",EDGE,{"derivedFrom":sQuery(id+"F17.wireOp",EDGE,"E68.14.1")}),-1.0]])]});
            var Q12;
            Q12=makeQuery(id+"F17.imprint","IMPRINT",FACE,{"disambiguationData":[TD([[makeQuery(id+"F17.imprint","IMPRINT",EDGE,{"derivedFrom":sQuery(id+"F17.wireOp",EDGE,"E68.7.1")}),-1.0]])]});
            var Q13;
            Q13=makeQuery(id+"F17.imprint","IMPRINT",FACE,{"disambiguationData":[TD([[makeQuery(id+"F17.imprint","IMPRINT",EDGE,{"derivedFrom":sQuery(id+"F17.wireOp",EDGE,"E68.4.1")}),-1.0]])]});
            var Q14;
            Q14=makeQuery(id+"F17.imprint","IMPRINT",FACE,{"disambiguationData":[TD([[makeQuery(id+"F17.imprint","IMPRINT",EDGE,{"derivedFrom":sQuery(id+"F17.wireOp",EDGE,"E68.11.1")}),-1.0]])]});
            var Q15;
            Q15=makeQuery(id+"F17.imprint","IMPRINT",FACE,{"disambiguationData":[TD([[makeQuery(id+"F17.imprint","IMPRINT",EDGE,{"derivedFrom":sQuery(id+"F17.wireOp",EDGE,"E68.15.1")}),-1.0]])]});
            var Q16;
            Q16=makeQuery(id+"F17.imprint","IMPRINT",FACE,{"disambiguationData":[TD([[makeQuery(id+"F17.imprint","IMPRINT",EDGE,{"derivedFrom":sQuery(id+"F17.wireOp",EDGE,"E68.9.1")}),-1.0]])]});
            extrude(context, id + "F18", {"entities" : qUnion([Q0, Q1, Q2, Q3, Q4, Q5, Q6, Q7, Q8, Q9, Q10, Q11, Q12, Q13, Q14, Q15, Q16]), "operationType" : NewBodyOperationType.ADD, "oppositeDirection" : true, "depth" : 17 * mm, "offsetDistance" : 25 * mm});
        }
        {
            var Q0;
            {var subQ0=sQuery(id+"F11.wireOp",EDGE,"E47");Q0=makeQuery(id+"F18.boolean.opBoolean","MERGE",FACE,{"derivedFrom":[makeQuery(id+"F12.opExtrude","CAP_FACE",FACE,{"disambiguationData":[OSD([subQ0])],"isStart":false}),makeQuery(id+"F18.opExtrude","CAP_FACE",FACE,{"disambiguationData":[OSD([subQ0,sQuery(id+"F17.wireOp",EDGE,"E59"),sQuery(id+"F17.wireOp",EDGE,"E60"),sQuery(id+"F17.wireOp",EDGE,"E61"),sQuery(id+"F17.wireOp",EDGE,"E62"),sQuery(id+"F17.wireOp",EDGE,"E63"),sQuery(id+"F17.wireOp",EDGE,"E64"),sQuery(id+"F17.wireOp",EDGE,"E65"),sQuery(id+"F17.wireOp",EDGE,"E66")])],"isStart":true}),makeQuery(id+"F18.opExtrude","CAP_FACE",FACE,{"disambiguationData":[OSD([subQ0,sQuery(id+"F17.wireOp",EDGE,"E68.1.1"),sQuery(id+"F17.wireOp",EDGE,"E68.1.2"),sQuery(id+"F17.wireOp",EDGE,"E68.1.3"),sQuery(id+"F17.wireOp",EDGE,"E68.1.4"),sQuery(id+"F17.wireOp",EDGE,"E68.1.5"),sQuery(id+"F17.wireOp",EDGE,"E68.1.6"),sQuery(id+"F17.wireOp",EDGE,"E68.1.7"),sQuery(id+"F17.wireOp",EDGE,"E68.1.8")])],"isStart":true}),makeQuery(id+"F18.opExtrude","CAP_FACE",FACE,{"disambiguationData":[OSD([subQ0,sQuery(id+"F17.wireOp",EDGE,"E68.2.1"),sQuery(id+"F17.wireOp",EDGE,"E68.2.2"),sQuery(id+"F17.wireOp",EDGE,"E68.2.3"),sQuery(id+"F17.wireOp",EDGE,"E68.2.4"),sQuery(id+"F17.wireOp",EDGE,"E68.2.5"),sQuery(id+"F17.wireOp",EDGE,"E68.2.6"),sQuery(id+"F17.wireOp",EDGE,"E68.2.7"),sQuery(id+"F17.wireOp",EDGE,"E68.2.8")])],"isStart":true}),makeQuery(id+"F18.opExtrude","CAP_FACE",FACE,{"disambiguationData":[OSD([subQ0,sQuery(id+"F17.wireOp",EDGE,"E68.3.1"),sQuery(id+"F17.wireOp",EDGE,"E68.3.2"),sQuery(id+"F17.wireOp",EDGE,"E68.3.3"),sQuery(id+"F17.wireOp",EDGE,"E68.3.4"),sQuery(id+"F17.wireOp",EDGE,"E68.3.5"),sQuery(id+"F17.wireOp",EDGE,"E68.3.6"),sQuery(id+"F17.wireOp",EDGE,"E68.3.7"),sQuery(id+"F17.wireOp",EDGE,"E68.3.8")])],"isStart":true}),makeQuery(id+"F18.opExtrude","CAP_FACE",FACE,{"disambiguationData":[OSD([subQ0,sQuery(id+"F17.wireOp",EDGE,"E68.4.1"),sQuery(id+"F17.wireOp",EDGE,"E68.4.2"),sQuery(id+"F17.wireOp",EDGE,"E68.4.3"),sQuery(id+"F17.wireOp",EDGE,"E68.4.4"),sQuery(id+"F17.wireOp",EDGE,"E68.4.5"),sQuery(id+"F17.wireOp",EDGE,"E68.4.6"),sQuery(id+"F17.wireOp",EDGE,"E68.4.7"),sQuery(id+"F17.wireOp",EDGE,"E68.4.8")])],"isStart":true}),makeQuery(id+"F18.opExtrude","CAP_FACE",FACE,{"disambiguationData":[OSD([subQ0,sQuery(id+"F17.wireOp",EDGE,"E68.5.1"),sQuery(id+"F17.wireOp",EDGE,"E68.5.2"),sQuery(id+"F17.wireOp",EDGE,"E68.5.3"),sQuery(id+"F17.wireOp",EDGE,"E68.5.4"),sQuery(id+"F17.wireOp",EDGE,"E68.5.5"),sQuery(id+"F17.wireOp",EDGE,"E68.5.6"),sQuery(id+"F17.wireOp",EDGE,"E68.5.7"),sQuery(id+"F17.wireOp",EDGE,"E68.5.8")])],"isStart":true}),makeQuery(id+"F18.opExtrude","CAP_FACE",FACE,{"disambiguationData":[OSD([subQ0,sQuery(id+"F17.wireOp",EDGE,"E68.6.1"),sQuery(id+"F17.wireOp",EDGE,"E68.6.2"),sQuery(id+"F17.wireOp",EDGE,"E68.6.3"),sQuery(id+"F17.wireOp",EDGE,"E68.6.4"),sQuery(id+"F17.wireOp",EDGE,"E68.6.5"),sQuery(id+"F17.wireOp",EDGE,"E68.6.6"),sQuery(id+"F17.wireOp",EDGE,"E68.6.7"),sQuery(id+"F17.wireOp",EDGE,"E68.6.8")])],"isStart":true}),makeQuery(id+"F18.opExtrude","CAP_FACE",FACE,{"disambiguationData":[OSD([subQ0,sQuery(id+"F17.wireOp",EDGE,"E68.7.1"),sQuery(id+"F17.wireOp",EDGE,"E68.7.2"),sQuery(id+"F17.wireOp",EDGE,"E68.7.3"),sQuery(id+"F17.wireOp",EDGE,"E68.7.4"),sQuery(id+"F17.wireOp",EDGE,"E68.7.5"),sQuery(id+"F17.wireOp",EDGE,"E68.7.6"),sQuery(id+"F17.wireOp",EDGE,"E68.7.7"),sQuery(id+"F17.wireOp",EDGE,"E68.7.8")])],"isStart":true}),makeQuery(id+"F18.opExtrude","CAP_FACE",FACE,{"disambiguationData":[OSD([subQ0,sQuery(id+"F17.wireOp",EDGE,"E68.8.1"),sQuery(id+"F17.wireOp",EDGE,"E68.8.2"),sQuery(id+"F17.wireOp",EDGE,"E68.8.3"),sQuery(id+"F17.wireOp",EDGE,"E68.8.4"),sQuery(id+"F17.wireOp",EDGE,"E68.8.5"),sQuery(id+"F17.wireOp",EDGE,"E68.8.6"),sQuery(id+"F17.wireOp",EDGE,"E68.8.7"),sQuery(id+"F17.wireOp",EDGE,"E68.8.8")])],"isStart":true}),makeQuery(id+"F18.opExtrude","CAP_FACE",FACE,{"disambiguationData":[OSD([subQ0,sQuery(id+"F17.wireOp",EDGE,"E68.9.1"),sQuery(id+"F17.wireOp",EDGE,"E68.9.2"),sQuery(id+"F17.wireOp",EDGE,"E68.9.3"),sQuery(id+"F17.wireOp",EDGE,"E68.9.4"),sQuery(id+"F17.wireOp",EDGE,"E68.9.5"),sQuery(id+"F17.wireOp",EDGE,"E68.9.6"),sQuery(id+"F17.wireOp",EDGE,"E68.9.7"),sQuery(id+"F17.wireOp",EDGE,"E68.9.8")])],"isStart":true}),makeQuery(id+"F18.opExtrude","CAP_FACE",FACE,{"disambiguationData":[OSD([subQ0,sQuery(id+"F17.wireOp",EDGE,"E68.10.1"),sQuery(id+"F17.wireOp",EDGE,"E68.10.2"),sQuery(id+"F17.wireOp",EDGE,"E68.10.3"),sQuery(id+"F17.wireOp",EDGE,"E68.10.4"),sQuery(id+"F17.wireOp",EDGE,"E68.10.5"),sQuery(id+"F17.wireOp",EDGE,"E68.10.6"),sQuery(id+"F17.wireOp",EDGE,"E68.10.7"),sQuery(id+"F17.wireOp",EDGE,"E68.10.8")])],"isStart":true}),makeQuery(id+"F18.opExtrude","CAP_FACE",FACE,{"disambiguationData":[OSD([subQ0,sQuery(id+"F17.wireOp",EDGE,"E68.11.1"),sQuery(id+"F17.wireOp",EDGE,"E68.11.2"),sQuery(id+"F17.wireOp",EDGE,"E68.11.3"),sQuery(id+"F17.wireOp",EDGE,"E68.11.4"),sQuery(id+"F17.wireOp",EDGE,"E68.11.5"),sQuery(id+"F17.wireOp",EDGE,"E68.11.6"),sQuery(id+"F17.wireOp",EDGE,"E68.11.7"),sQuery(id+"F17.wireOp",EDGE,"E68.11.8")])],"isStart":true}),makeQuery(id+"F18.opExtrude","CAP_FACE",FACE,{"disambiguationData":[OSD([subQ0,sQuery(id+"F17.wireOp",EDGE,"E68.12.1"),sQuery(id+"F17.wireOp",EDGE,"E68.12.2"),sQuery(id+"F17.wireOp",EDGE,"E68.12.3"),sQuery(id+"F17.wireOp",EDGE,"E68.12.4"),sQuery(id+"F17.wireOp",EDGE,"E68.12.5"),sQuery(id+"F17.wireOp",EDGE,"E68.12.6"),sQuery(id+"F17.wireOp",EDGE,"E68.12.7"),sQuery(id+"F17.wireOp",EDGE,"E68.12.8")])],"isStart":true}),makeQuery(id+"F18.opExtrude","CAP_FACE",FACE,{"disambiguationData":[OSD([subQ0,sQuery(id+"F17.wireOp",EDGE,"E68.13.1"),sQuery(id+"F17.wireOp",EDGE,"E68.13.2"),sQuery(id+"F17.wireOp",EDGE,"E68.13.3"),sQuery(id+"F17.wireOp",EDGE,"E68.13.4"),sQuery(id+"F17.wireOp",EDGE,"E68.13.5"),sQuery(id+"F17.wireOp",EDGE,"E68.13.6"),sQuery(id+"F17.wireOp",EDGE,"E68.13.7"),sQuery(id+"F17.wireOp",EDGE,"E68.13.8")])],"isStart":true}),makeQuery(id+"F18.opExtrude","CAP_FACE",FACE,{"disambiguationData":[OSD([subQ0,sQuery(id+"F17.wireOp",EDGE,"E68.14.1"),sQuery(id+"F17.wireOp",EDGE,"E68.14.2"),sQuery(id+"F17.wireOp",EDGE,"E68.14.3"),sQuery(id+"F17.wireOp",EDGE,"E68.14.4"),sQuery(id+"F17.wireOp",EDGE,"E68.14.5"),sQuery(id+"F17.wireOp",EDGE,"E68.14.6"),sQuery(id+"F17.wireOp",EDGE,"E68.14.7"),sQuery(id+"F17.wireOp",EDGE,"E68.14.8")])],"isStart":true}),makeQuery(id+"F18.opExtrude","CAP_FACE",FACE,{"disambiguationData":[OSD([subQ0,sQuery(id+"F17.wireOp",EDGE,"E68.15.1"),sQuery(id+"F17.wireOp",EDGE,"E68.15.2"),sQuery(id+"F17.wireOp",EDGE,"E68.15.3"),sQuery(id+"F17.wireOp",EDGE,"E68.15.4"),sQuery(id+"F17.wireOp",EDGE,"E68.15.5"),sQuery(id+"F17.wireOp",EDGE,"E68.15.6"),sQuery(id+"F17.wireOp",EDGE,"E68.15.7"),sQuery(id+"F17.wireOp",EDGE,"E68.15.8")])],"isStart":true})]});}
            var sketch = newSketch(context, id + "F19", { "sketchPlane" : qUnion([Q0])});
            skArc(sketch, "E69", {"start": v(-8.15, 30.43) * mm, "mid": v(-6.15, 30.9) * mm, "end": v(-4.11, 31.23) * mm});
            skArc(sketch, "E70", {"start": v(-8.9, 33.2) * mm, "mid": v(-6.7, 33.71) * mm, "end": v(-4.49, 34.08) * mm});
            skLineSegment(sketch, "E71", {"start": v(-8.9, 33.2) * mm, "end": v(-8.15, 30.43) * mm});
            skLineSegment(sketch, "E72", {"start": v(-4.49, 34.08) * mm, "end": v(-4.11, 31.23) * mm});
            skArc(sketch, "E73.1.0", {"start": v(-19.18, 25) * mm, "mid": v(-17.5, 26.2) * mm, "end": v(-15.75, 27.28) * mm});
            skLineSegment(sketch, "E73.1.1", {"start": v(-20.93, 27.27) * mm, "end": v(-19.18, 25) * mm});
            skArc(sketch, "E73.1.2", {"start": v(-20.93, 27.27) * mm, "mid": v(-19.1, 28.58) * mm, "end": v(-17.19, 29.77) * mm});
            skLineSegment(sketch, "E73.1.3", {"start": v(-17.19, 29.77) * mm, "end": v(-15.75, 27.28) * mm});
            skArc(sketch, "E73.2.0", {"start": v(-27.28, 15.75) * mm, "mid": v(-26.2, 17.5) * mm, "end": v(-25, 19.18) * mm});
            skLineSegment(sketch, "E73.2.1", {"start": v(-29.77, 17.19) * mm, "end": v(-27.28, 15.75) * mm});
            skArc(sketch, "E73.2.2", {"start": v(-29.77, 17.19) * mm, "mid": v(-28.58, 19.1) * mm, "end": v(-27.27, 20.93) * mm});
            skLineSegment(sketch, "E73.2.3", {"start": v(-27.27, 20.93) * mm, "end": v(-25, 19.18) * mm});
            skArc(sketch, "E73.3.0", {"start": v(-31.23, 4.11) * mm, "mid": v(-30.9, 6.15) * mm, "end": v(-30.43, 8.15) * mm});
            skLineSegment(sketch, "E73.3.1", {"start": v(-34.08, 4.49) * mm, "end": v(-31.23, 4.11) * mm});
            skArc(sketch, "E73.3.2", {"start": v(-34.08, 4.49) * mm, "mid": v(-33.71, 6.7) * mm, "end": v(-33.2, 8.9) * mm});
            skLineSegment(sketch, "E73.3.3", {"start": v(-33.2, 8.9) * mm, "end": v(-30.43, 8.15) * mm});
            skArc(sketch, "E73.4.0", {"start": v(-30.43, -8.15) * mm, "mid": v(-30.9, -6.15) * mm, "end": v(-31.23, -4.11) * mm});
            skLineSegment(sketch, "E73.4.1", {"start": v(-33.2, -8.9) * mm, "end": v(-30.43, -8.15) * mm});
            skArc(sketch, "E73.4.2", {"start": v(-33.2, -8.9) * mm, "mid": v(-33.71, -6.7) * mm, "end": v(-34.08, -4.49) * mm});
            skLineSegment(sketch, "E73.4.3", {"start": v(-34.08, -4.49) * mm, "end": v(-31.23, -4.11) * mm});
            skArc(sketch, "E73.5.0", {"start": v(-25, -19.18) * mm, "mid": v(-26.2, -17.5) * mm, "end": v(-27.28, -15.75) * mm});
            skLineSegment(sketch, "E73.5.1", {"start": v(-27.27, -20.93) * mm, "end": v(-25, -19.18) * mm});
            skArc(sketch, "E73.5.2", {"start": v(-27.27, -20.93) * mm, "mid": v(-28.58, -19.1) * mm, "end": v(-29.77, -17.19) * mm});
            skLineSegment(sketch, "E73.5.3", {"start": v(-29.77, -17.19) * mm, "end": v(-27.28, -15.75) * mm});
            skArc(sketch, "E73.6.0", {"start": v(-15.75, -27.28) * mm, "mid": v(-17.5, -26.2) * mm, "end": v(-19.18, -25) * mm});
            skLineSegment(sketch, "E73.6.1", {"start": v(-17.19, -29.77) * mm, "end": v(-15.75, -27.28) * mm});
            skArc(sketch, "E73.6.2", {"start": v(-17.19, -29.77) * mm, "mid": v(-19.1, -28.58) * mm, "end": v(-20.93, -27.27) * mm});
            skLineSegment(sketch, "E73.6.3", {"start": v(-20.93, -27.27) * mm, "end": v(-19.18, -25) * mm});
            skArc(sketch, "E73.7.0", {"start": v(-4.11, -31.23) * mm, "mid": v(-6.15, -30.9) * mm, "end": v(-8.15, -30.43) * mm});
            skLineSegment(sketch, "E73.7.1", {"start": v(-4.49, -34.08) * mm, "end": v(-4.11, -31.23) * mm});
            skArc(sketch, "E73.7.2", {"start": v(-4.49, -34.08) * mm, "mid": v(-6.7, -33.71) * mm, "end": v(-8.9, -33.2) * mm});
            skLineSegment(sketch, "E73.7.3", {"start": v(-8.9, -33.2) * mm, "end": v(-8.15, -30.43) * mm});
            skArc(sketch, "E73.8.0", {"start": v(8.15, -30.43) * mm, "mid": v(6.15, -30.9) * mm, "end": v(4.11, -31.23) * mm});
            skLineSegment(sketch, "E73.8.1", {"start": v(8.9, -33.2) * mm, "end": v(8.15, -30.43) * mm});
            skArc(sketch, "E73.8.2", {"start": v(8.9, -33.2) * mm, "mid": v(6.7, -33.71) * mm, "end": v(4.49, -34.08) * mm});
            skLineSegment(sketch, "E73.8.3", {"start": v(4.49, -34.08) * mm, "end": v(4.11, -31.23) * mm});
            skArc(sketch, "E73.9.0", {"start": v(19.18, -25) * mm, "mid": v(17.5, -26.2) * mm, "end": v(15.75, -27.28) * mm});
            skLineSegment(sketch, "E73.9.1", {"start": v(20.93, -27.27) * mm, "end": v(19.18, -25) * mm});
            skArc(sketch, "E73.9.2", {"start": v(20.93, -27.27) * mm, "mid": v(19.1, -28.58) * mm, "end": v(17.19, -29.77) * mm});
            skLineSegment(sketch, "E73.9.3", {"start": v(17.19, -29.77) * mm, "end": v(15.75, -27.28) * mm});
            skArc(sketch, "E73.10.0", {"start": v(27.28, -15.75) * mm, "mid": v(26.2, -17.5) * mm, "end": v(25, -19.18) * mm});
            skLineSegment(sketch, "E73.10.1", {"start": v(29.77, -17.19) * mm, "end": v(27.28, -15.75) * mm});
            skArc(sketch, "E73.10.2", {"start": v(29.77, -17.19) * mm, "mid": v(28.58, -19.1) * mm, "end": v(27.27, -20.93) * mm});
            skLineSegment(sketch, "E73.10.3", {"start": v(27.27, -20.93) * mm, "end": v(25, -19.18) * mm});
            skArc(sketch, "E73.11.0", {"start": v(31.23, -4.11) * mm, "mid": v(30.9, -6.15) * mm, "end": v(30.43, -8.15) * mm});
            skLineSegment(sketch, "E73.11.1", {"start": v(34.08, -4.49) * mm, "end": v(31.23, -4.11) * mm});
            skArc(sketch, "E73.11.2", {"start": v(34.08, -4.49) * mm, "mid": v(33.71, -6.7) * mm, "end": v(33.2, -8.9) * mm});
            skLineSegment(sketch, "E73.11.3", {"start": v(33.2, -8.9) * mm, "end": v(30.43, -8.15) * mm});
            skArc(sketch, "E73.12.0", {"start": v(30.43, 8.15) * mm, "mid": v(30.9, 6.15) * mm, "end": v(31.23, 4.11) * mm});
            skLineSegment(sketch, "E73.12.1", {"start": v(33.2, 8.9) * mm, "end": v(30.43, 8.15) * mm});
            skArc(sketch, "E73.12.2", {"start": v(33.2, 8.9) * mm, "mid": v(33.71, 6.7) * mm, "end": v(34.08, 4.49) * mm});
            skLineSegment(sketch, "E73.12.3", {"start": v(34.08, 4.49) * mm, "end": v(31.23, 4.11) * mm});
            skArc(sketch, "E73.13.0", {"start": v(25, 19.18) * mm, "mid": v(26.2, 17.5) * mm, "end": v(27.28, 15.75) * mm});
            skLineSegment(sketch, "E73.13.1", {"start": v(27.27, 20.93) * mm, "end": v(25, 19.18) * mm});
            skArc(sketch, "E73.13.2", {"start": v(27.27, 20.93) * mm, "mid": v(28.58, 19.1) * mm, "end": v(29.77, 17.19) * mm});
            skLineSegment(sketch, "E73.13.3", {"start": v(29.77, 17.19) * mm, "end": v(27.28, 15.75) * mm});
            skArc(sketch, "E73.14.0", {"start": v(15.75, 27.28) * mm, "mid": v(17.5, 26.2) * mm, "end": v(19.18, 25) * mm});
            skLineSegment(sketch, "E73.14.1", {"start": v(17.19, 29.77) * mm, "end": v(15.75, 27.28) * mm});
            skArc(sketch, "E73.14.2", {"start": v(17.19, 29.77) * mm, "mid": v(19.1, 28.58) * mm, "end": v(20.93, 27.27) * mm});
            skLineSegment(sketch, "E73.14.3", {"start": v(20.93, 27.27) * mm, "end": v(19.18, 25) * mm});
            skArc(sketch, "E73.15.0", {"start": v(4.11, 31.23) * mm, "mid": v(6.15, 30.9) * mm, "end": v(8.15, 30.43) * mm});
            skLineSegment(sketch, "E73.15.1", {"start": v(4.49, 34.08) * mm, "end": v(4.11, 31.23) * mm});
            skArc(sketch, "E73.15.2", {"start": v(4.49, 34.08) * mm, "mid": v(6.7, 33.71) * mm, "end": v(8.9, 33.2) * mm});
            skLineSegment(sketch, "E73.15.3", {"start": v(8.9, 33.2) * mm, "end": v(8.15, 30.43) * mm});
            skSolve(sketch);
        }
        {
            var Q0;
            Q0 = qSketchRegion(id + "F19", true);
            extrude(context, id + "F20", {"entities" : qUnion([Q0]), "operationType" : NewBodyOperationType.REMOVE, "oppositeDirection" : true, "depth" : 5 * mm, "offsetDistance" : 25 * mm});
        }
        {
            var Q0;
            {var subQ0=sQuery(id+"F11.wireOp",EDGE,"E47");Q0=makeQuery(id+"F18.boolean.opBoolean","MERGE",FACE,{"derivedFrom":[makeQuery(id+"F12.opExtrude","CAP_FACE",FACE,{"disambiguationData":[OSD([subQ0])],"isStart":false}),makeQuery(id+"F18.opExtrude","CAP_FACE",FACE,{"disambiguationData":[OSD([subQ0,sQuery(id+"F17.wireOp",EDGE,"E59"),sQuery(id+"F17.wireOp",EDGE,"E60"),sQuery(id+"F17.wireOp",EDGE,"E61"),sQuery(id+"F17.wireOp",EDGE,"E62"),sQuery(id+"F17.wireOp",EDGE,"E63"),sQuery(id+"F17.wireOp",EDGE,"E64"),sQuery(id+"F17.wireOp",EDGE,"E65"),sQuery(id+"F17.wireOp",EDGE,"E66")])],"isStart":true}),makeQuery(id+"F18.opExtrude","CAP_FACE",FACE,{"disambiguationData":[OSD([subQ0,sQuery(id+"F17.wireOp",EDGE,"E68.1.1"),sQuery(id+"F17.wireOp",EDGE,"E68.1.2"),sQuery(id+"F17.wireOp",EDGE,"E68.1.3"),sQuery(id+"F17.wireOp",EDGE,"E68.1.4"),sQuery(id+"F17.wireOp",EDGE,"E68.1.5"),sQuery(id+"F17.wireOp",EDGE,"E68.1.6"),sQuery(id+"F17.wireOp",EDGE,"E68.1.7"),sQuery(id+"F17.wireOp",EDGE,"E68.1.8")])],"isStart":true}),makeQuery(id+"F18.opExtrude","CAP_FACE",FACE,{"disambiguationData":[OSD([subQ0,sQuery(id+"F17.wireOp",EDGE,"E68.2.1"),sQuery(id+"F17.wireOp",EDGE,"E68.2.2"),sQuery(id+"F17.wireOp",EDGE,"E68.2.3"),sQuery(id+"F17.wireOp",EDGE,"E68.2.4"),sQuery(id+"F17.wireOp",EDGE,"E68.2.5"),sQuery(id+"F17.wireOp",EDGE,"E68.2.6"),sQuery(id+"F17.wireOp",EDGE,"E68.2.7"),sQuery(id+"F17.wireOp",EDGE,"E68.2.8")])],"isStart":true}),makeQuery(id+"F18.opExtrude","CAP_FACE",FACE,{"disambiguationData":[OSD([subQ0,sQuery(id+"F17.wireOp",EDGE,"E68.3.1"),sQuery(id+"F17.wireOp",EDGE,"E68.3.2"),sQuery(id+"F17.wireOp",EDGE,"E68.3.3"),sQuery(id+"F17.wireOp",EDGE,"E68.3.4"),sQuery(id+"F17.wireOp",EDGE,"E68.3.5"),sQuery(id+"F17.wireOp",EDGE,"E68.3.6"),sQuery(id+"F17.wireOp",EDGE,"E68.3.7"),sQuery(id+"F17.wireOp",EDGE,"E68.3.8")])],"isStart":true}),makeQuery(id+"F18.opExtrude","CAP_FACE",FACE,{"disambiguationData":[OSD([subQ0,sQuery(id+"F17.wireOp",EDGE,"E68.4.1"),sQuery(id+"F17.wireOp",EDGE,"E68.4.2"),sQuery(id+"F17.wireOp",EDGE,"E68.4.3"),sQuery(id+"F17.wireOp",EDGE,"E68.4.4"),sQuery(id+"F17.wireOp",EDGE,"E68.4.5"),sQuery(id+"F17.wireOp",EDGE,"E68.4.6"),sQuery(id+"F17.wireOp",EDGE,"E68.4.7"),sQuery(id+"F17.wireOp",EDGE,"E68.4.8")])],"isStart":true}),makeQuery(id+"F18.opExtrude","CAP_FACE",FACE,{"disambiguationData":[OSD([subQ0,sQuery(id+"F17.wireOp",EDGE,"E68.5.1"),sQuery(id+"F17.wireOp",EDGE,"E68.5.2"),sQuery(id+"F17.wireOp",EDGE,"E68.5.3"),sQuery(id+"F17.wireOp",EDGE,"E68.5.4"),sQuery(id+"F17.wireOp",EDGE,"E68.5.5"),sQuery(id+"F17.wireOp",EDGE,"E68.5.6"),sQuery(id+"F17.wireOp",EDGE,"E68.5.7"),sQuery(id+"F17.wireOp",EDGE,"E68.5.8")])],"isStart":true}),makeQuery(id+"F18.opExtrude","CAP_FACE",FACE,{"disambiguationData":[OSD([subQ0,sQuery(id+"F17.wireOp",EDGE,"E68.6.1"),sQuery(id+"F17.wireOp",EDGE,"E68.6.2"),sQuery(id+"F17.wireOp",EDGE,"E68.6.3"),sQuery(id+"F17.wireOp",EDGE,"E68.6.4"),sQuery(id+"F17.wireOp",EDGE,"E68.6.5"),sQuery(id+"F17.wireOp",EDGE,"E68.6.6"),sQuery(id+"F17.wireOp",EDGE,"E68.6.7"),sQuery(id+"F17.wireOp",EDGE,"E68.6.8")])],"isStart":true}),makeQuery(id+"F18.opExtrude","CAP_FACE",FACE,{"disambiguationData":[OSD([subQ0,sQuery(id+"F17.wireOp",EDGE,"E68.7.1"),sQuery(id+"F17.wireOp",EDGE,"E68.7.2"),sQuery(id+"F17.wireOp",EDGE,"E68.7.3"),sQuery(id+"F17.wireOp",EDGE,"E68.7.4"),sQuery(id+"F17.wireOp",EDGE,"E68.7.5"),sQuery(id+"F17.wireOp",EDGE,"E68.7.6"),sQuery(id+"F17.wireOp",EDGE,"E68.7.7"),sQuery(id+"F17.wireOp",EDGE,"E68.7.8")])],"isStart":true}),makeQuery(id+"F18.opExtrude","CAP_FACE",FACE,{"disambiguationData":[OSD([subQ0,sQuery(id+"F17.wireOp",EDGE,"E68.8.1"),sQuery(id+"F17.wireOp",EDGE,"E68.8.2"),sQuery(id+"F17.wireOp",EDGE,"E68.8.3"),sQuery(id+"F17.wireOp",EDGE,"E68.8.4"),sQuery(id+"F17.wireOp",EDGE,"E68.8.5"),sQuery(id+"F17.wireOp",EDGE,"E68.8.6"),sQuery(id+"F17.wireOp",EDGE,"E68.8.7"),sQuery(id+"F17.wireOp",EDGE,"E68.8.8")])],"isStart":true}),makeQuery(id+"F18.opExtrude","CAP_FACE",FACE,{"disambiguationData":[OSD([subQ0,sQuery(id+"F17.wireOp",EDGE,"E68.9.1"),sQuery(id+"F17.wireOp",EDGE,"E68.9.2"),sQuery(id+"F17.wireOp",EDGE,"E68.9.3"),sQuery(id+"F17.wireOp",EDGE,"E68.9.4"),sQuery(id+"F17.wireOp",EDGE,"E68.9.5"),sQuery(id+"F17.wireOp",EDGE,"E68.9.6"),sQuery(id+"F17.wireOp",EDGE,"E68.9.7"),sQuery(id+"F17.wireOp",EDGE,"E68.9.8")])],"isStart":true}),makeQuery(id+"F18.opExtrude","CAP_FACE",FACE,{"disambiguationData":[OSD([subQ0,sQuery(id+"F17.wireOp",EDGE,"E68.10.1"),sQuery(id+"F17.wireOp",EDGE,"E68.10.2"),sQuery(id+"F17.wireOp",EDGE,"E68.10.3"),sQuery(id+"F17.wireOp",EDGE,"E68.10.4"),sQuery(id+"F17.wireOp",EDGE,"E68.10.5"),sQuery(id+"F17.wireOp",EDGE,"E68.10.6"),sQuery(id+"F17.wireOp",EDGE,"E68.10.7"),sQuery(id+"F17.wireOp",EDGE,"E68.10.8")])],"isStart":true}),makeQuery(id+"F18.opExtrude","CAP_FACE",FACE,{"disambiguationData":[OSD([subQ0,sQuery(id+"F17.wireOp",EDGE,"E68.11.1"),sQuery(id+"F17.wireOp",EDGE,"E68.11.2"),sQuery(id+"F17.wireOp",EDGE,"E68.11.3"),sQuery(id+"F17.wireOp",EDGE,"E68.11.4"),sQuery(id+"F17.wireOp",EDGE,"E68.11.5"),sQuery(id+"F17.wireOp",EDGE,"E68.11.6"),sQuery(id+"F17.wireOp",EDGE,"E68.11.7"),sQuery(id+"F17.wireOp",EDGE,"E68.11.8")])],"isStart":true}),makeQuery(id+"F18.opExtrude","CAP_FACE",FACE,{"disambiguationData":[OSD([subQ0,sQuery(id+"F17.wireOp",EDGE,"E68.12.1"),sQuery(id+"F17.wireOp",EDGE,"E68.12.2"),sQuery(id+"F17.wireOp",EDGE,"E68.12.3"),sQuery(id+"F17.wireOp",EDGE,"E68.12.4"),sQuery(id+"F17.wireOp",EDGE,"E68.12.5"),sQuery(id+"F17.wireOp",EDGE,"E68.12.6"),sQuery(id+"F17.wireOp",EDGE,"E68.12.7"),sQuery(id+"F17.wireOp",EDGE,"E68.12.8")])],"isStart":true}),makeQuery(id+"F18.opExtrude","CAP_FACE",FACE,{"disambiguationData":[OSD([subQ0,sQuery(id+"F17.wireOp",EDGE,"E68.13.1"),sQuery(id+"F17.wireOp",EDGE,"E68.13.2"),sQuery(id+"F17.wireOp",EDGE,"E68.13.3"),sQuery(id+"F17.wireOp",EDGE,"E68.13.4"),sQuery(id+"F17.wireOp",EDGE,"E68.13.5"),sQuery(id+"F17.wireOp",EDGE,"E68.13.6"),sQuery(id+"F17.wireOp",EDGE,"E68.13.7"),sQuery(id+"F17.wireOp",EDGE,"E68.13.8")])],"isStart":true}),makeQuery(id+"F18.opExtrude","CAP_FACE",FACE,{"disambiguationData":[OSD([subQ0,sQuery(id+"F17.wireOp",EDGE,"E68.14.1"),sQuery(id+"F17.wireOp",EDGE,"E68.14.2"),sQuery(id+"F17.wireOp",EDGE,"E68.14.3"),sQuery(id+"F17.wireOp",EDGE,"E68.14.4"),sQuery(id+"F17.wireOp",EDGE,"E68.14.5"),sQuery(id+"F17.wireOp",EDGE,"E68.14.6"),sQuery(id+"F17.wireOp",EDGE,"E68.14.7"),sQuery(id+"F17.wireOp",EDGE,"E68.14.8")])],"isStart":true}),makeQuery(id+"F18.opExtrude","CAP_FACE",FACE,{"disambiguationData":[OSD([subQ0,sQuery(id+"F17.wireOp",EDGE,"E68.15.1"),sQuery(id+"F17.wireOp",EDGE,"E68.15.2"),sQuery(id+"F17.wireOp",EDGE,"E68.15.3"),sQuery(id+"F17.wireOp",EDGE,"E68.15.4"),sQuery(id+"F17.wireOp",EDGE,"E68.15.5"),sQuery(id+"F17.wireOp",EDGE,"E68.15.6"),sQuery(id+"F17.wireOp",EDGE,"E68.15.7"),sQuery(id+"F17.wireOp",EDGE,"E68.15.8")])],"isStart":true})]});}
            var sketch = newSketch(context, id + "F21", { "sketchPlane" : qUnion([Q0])});
            skCircle(sketch, "E74.0.3.0", {"center": v(-22.52, -14.76) * mm, "radius": 1.25 * mm});
            skCircle(sketch, "E74.0.4.0", {"center": v(-23.5, -9.86) * mm, "radius": 1.25 * mm});
            skCircle(sketch, "E74.0.5.0", {"center": v(-24.5, -4.96) * mm, "radius": 1.25 * mm});
            skCircle(sketch, "E74.0.6.0", {"center": v(-25.5, -0.06) * mm, "radius": 1.25 * mm});
            skCircle(sketch, "E74.0.7.0", {"center": v(-26.49, 4.84) * mm, "radius": 1.25 * mm});
            skCircle(sketch, "E74.1.2.0", {"center": v(-16.62, -18.67) * mm, "radius": 1.25 * mm});
            skCircle(sketch, "E74.1.3.0", {"center": v(-17.62, -13.77) * mm, "radius": 1.25 * mm});
            skCircle(sketch, "E74.1.4.0", {"center": v(-18.6, -8.87) * mm, "radius": 1.25 * mm});
            skCircle(sketch, "E74.1.5.0", {"center": v(-19.6, -3.97) * mm, "radius": 1.25 * mm});
            skCircle(sketch, "E74.1.6.0", {"center": v(-20.6, 0.93) * mm, "radius": 1.25 * mm});
            skCircle(sketch, "E74.1.7.0", {"center": v(-21.59, 5.83) * mm, "radius": 1.25 * mm});
            skCircle(sketch, "E74.1.8.0", {"center": v(-22.58, 10.73) * mm, "radius": 1.25 * mm});
            skCircle(sketch, "E74.2.1.0", {"center": v(-10.73, -22.58) * mm, "radius": 1.25 * mm});
            skCircle(sketch, "E74.2.2.0", {"center": v(-11.72, -17.68) * mm, "radius": 1.25 * mm});
            skCircle(sketch, "E74.2.3.0", {"center": v(-12.72, -12.78) * mm, "radius": 1.25 * mm});
            skCircle(sketch, "E74.2.4.0", {"center": v(-13.7, -7.88) * mm, "radius": 1.25 * mm});
            skCircle(sketch, "E74.2.5.0", {"center": v(-14.7, -2.98) * mm, "radius": 1.25 * mm});
            skCircle(sketch, "E74.2.6.0", {"center": v(-15.7, 1.92) * mm, "radius": 1.25 * mm});
            skCircle(sketch, "E74.2.7.0", {"center": v(-16.69, 6.82) * mm, "radius": 1.25 * mm});
            skCircle(sketch, "E74.2.8.0", {"center": v(-17.68, 11.72) * mm, "radius": 1.25 * mm});
            skCircle(sketch, "E74.2.9.0", {"center": v(-18.67, 16.62) * mm, "radius": 1.25 * mm});
            skCircle(sketch, "E74.3.0.0", {"center": v(-4.84, -26.49) * mm, "radius": 1.25 * mm});
            skCircle(sketch, "E74.3.1.0", {"center": v(-5.83, -21.59) * mm, "radius": 1.25 * mm});
            skCircle(sketch, "E74.3.2.0", {"center": v(-6.82, -16.69) * mm, "radius": 1.25 * mm});
            skCircle(sketch, "E74.3.3.0", {"center": v(-7.82, -11.79) * mm, "radius": 1.25 * mm});
            skCircle(sketch, "E74.3.4.0", {"center": v(-8.8, -6.89) * mm, "radius": 1.25 * mm});
            skCircle(sketch, "E74.3.5.0", {"center": v(-9.8, -1.99) * mm, "radius": 1.25 * mm});
            skCircle(sketch, "E74.3.6.0", {"center": v(-10.8, 2.91) * mm, "radius": 1.25 * mm});
            skCircle(sketch, "E74.3.7.0", {"center": v(-11.79, 7.82) * mm, "radius": 1.25 * mm});
            skCircle(sketch, "E74.3.8.0", {"center": v(-12.78, 12.72) * mm, "radius": 1.25 * mm});
            skCircle(sketch, "E74.3.9.0", {"center": v(-13.77, 17.62) * mm, "radius": 1.25 * mm});
            skCircle(sketch, "E74.3.10.0", {"center": v(-14.76, 22.52) * mm, "radius": 1.25 * mm});
            skCircle(sketch, "E74.4.0.0", {"center": v(0.06, -25.5) * mm, "radius": 1.25 * mm});
            skCircle(sketch, "E74.4.1.0", {"center": v(-0.93, -20.6) * mm, "radius": 1.25 * mm});
            skCircle(sketch, "E74.4.2.0", {"center": v(-1.92, -15.7) * mm, "radius": 1.25 * mm});
            skCircle(sketch, "E74.4.3.0", {"center": v(-2.91, -10.8) * mm, "radius": 1.25 * mm});
            skCircle(sketch, "E74.4.4.0", {"center": v(-3.9, -5.9) * mm, "radius": 1.25 * mm});
            skCircle(sketch, "E74.4.5.0", {"center": v(-4.9, -1) * mm, "radius": 1.25 * mm});
            skCircle(sketch, "E74.4.6.0", {"center": v(-5.9, 3.9) * mm, "radius": 1.25 * mm});
            skCircle(sketch, "E74.4.7.0", {"center": v(-6.89, 8.8) * mm, "radius": 1.25 * mm});
            skCircle(sketch, "E74.4.8.0", {"center": v(-7.88, 13.7) * mm, "radius": 1.25 * mm});
            skCircle(sketch, "E74.4.9.0", {"center": v(-8.87, 18.6) * mm, "radius": 1.25 * mm});
            skCircle(sketch, "E74.4.10.0", {"center": v(-9.86, 23.5) * mm, "radius": 1.25 * mm});
            skCircle(sketch, "E74.5.0.0", {"center": v(4.96, -24.5) * mm, "radius": 1.25 * mm});
            skCircle(sketch, "E74.5.1.0", {"center": v(3.97, -19.6) * mm, "radius": 1.25 * mm});
            skCircle(sketch, "E74.5.2.0", {"center": v(2.98, -14.7) * mm, "radius": 1.25 * mm});
            skCircle(sketch, "E74.5.3.0", {"center": v(1.99, -9.8) * mm, "radius": 1.25 * mm});
            skCircle(sketch, "E74.5.4.0", {"center": v(1, -4.9) * mm, "radius": 1.25 * mm});
            skCircle(sketch, "E74.5.5.0", {"center": v(0, 0) * mm, "radius": 1.25 * mm});
            skCircle(sketch, "E74.5.6.0", {"center": v(-1, 4.9) * mm, "radius": 1.25 * mm});
            skCircle(sketch, "E74.5.7.0", {"center": v(-1.99, 9.8) * mm, "radius": 1.25 * mm});
            skCircle(sketch, "E74.5.8.0", {"center": v(-2.98, 14.7) * mm, "radius": 1.25 * mm});
            skCircle(sketch, "E74.5.9.0", {"center": v(-3.97, 19.6) * mm, "radius": 1.25 * mm});
            skCircle(sketch, "E74.5.10.0", {"center": v(-4.96, 24.5) * mm, "radius": 1.25 * mm});
            skCircle(sketch, "E74.6.0.0", {"center": v(9.86, -23.5) * mm, "radius": 1.25 * mm});
            skCircle(sketch, "E74.6.1.0", {"center": v(8.87, -18.6) * mm, "radius": 1.25 * mm});
            skCircle(sketch, "E74.6.2.0", {"center": v(7.88, -13.7) * mm, "radius": 1.25 * mm});
            skCircle(sketch, "E74.6.3.0", {"center": v(6.89, -8.8) * mm, "radius": 1.25 * mm});
            skCircle(sketch, "E74.6.4.0", {"center": v(5.9, -3.9) * mm, "radius": 1.25 * mm});
            skCircle(sketch, "E74.6.5.0", {"center": v(4.9, 1) * mm, "radius": 1.25 * mm});
            skCircle(sketch, "E74.6.6.0", {"center": v(3.9, 5.9) * mm, "radius": 1.25 * mm});
            skCircle(sketch, "E74.6.7.0", {"center": v(2.91, 10.8) * mm, "radius": 1.25 * mm});
            skCircle(sketch, "E74.6.8.0", {"center": v(1.92, 15.7) * mm, "radius": 1.25 * mm});
            skCircle(sketch, "E74.6.9.0", {"center": v(0.93, 20.6) * mm, "radius": 1.25 * mm});
            skCircle(sketch, "E74.6.10.0", {"center": v(-0.06, 25.5) * mm, "radius": 1.25 * mm});
            skCircle(sketch, "E74.7.0.0", {"center": v(14.76, -22.52) * mm, "radius": 1.25 * mm});
            skCircle(sketch, "E74.7.1.0", {"center": v(13.77, -17.62) * mm, "radius": 1.25 * mm});
            skCircle(sketch, "E74.7.2.0", {"center": v(12.78, -12.72) * mm, "radius": 1.25 * mm});
            skCircle(sketch, "E74.7.3.0", {"center": v(11.79, -7.82) * mm, "radius": 1.25 * mm});
            skCircle(sketch, "E74.7.4.0", {"center": v(10.8, -2.91) * mm, "radius": 1.25 * mm});
            skCircle(sketch, "E74.7.5.0", {"center": v(9.8, 1.99) * mm, "radius": 1.25 * mm});
            skCircle(sketch, "E74.7.6.0", {"center": v(8.8, 6.89) * mm, "radius": 1.25 * mm});
            skCircle(sketch, "E74.7.7.0", {"center": v(7.82, 11.79) * mm, "radius": 1.25 * mm});
            skCircle(sketch, "E74.7.8.0", {"center": v(6.82, 16.69) * mm, "radius": 1.25 * mm});
            skCircle(sketch, "E74.7.9.0", {"center": v(5.83, 21.59) * mm, "radius": 1.25 * mm});
            skCircle(sketch, "E74.7.10.0", {"center": v(4.84, 26.49) * mm, "radius": 1.25 * mm});
            skCircle(sketch, "E74.8.1.0", {"center": v(18.67, -16.62) * mm, "radius": 1.25 * mm});
            skCircle(sketch, "E74.8.2.0", {"center": v(17.68, -11.72) * mm, "radius": 1.25 * mm});
            skCircle(sketch, "E74.8.3.0", {"center": v(16.69, -6.82) * mm, "radius": 1.25 * mm});
            skCircle(sketch, "E74.8.4.0", {"center": v(15.7, -1.92) * mm, "radius": 1.25 * mm});
            skCircle(sketch, "E74.8.5.0", {"center": v(14.7, 2.98) * mm, "radius": 1.25 * mm});
            skCircle(sketch, "E74.8.6.0", {"center": v(13.7, 7.88) * mm, "radius": 1.25 * mm});
            skCircle(sketch, "E74.8.7.0", {"center": v(12.72, 12.78) * mm, "radius": 1.25 * mm});
            skCircle(sketch, "E74.8.8.0", {"center": v(11.72, 17.68) * mm, "radius": 1.25 * mm});
            skCircle(sketch, "E74.8.9.0", {"center": v(10.73, 22.58) * mm, "radius": 1.25 * mm});
            skCircle(sketch, "E74.9.2.0", {"center": v(22.58, -10.73) * mm, "radius": 1.25 * mm});
            skCircle(sketch, "E74.9.3.0", {"center": v(21.59, -5.83) * mm, "radius": 1.25 * mm});
            skCircle(sketch, "E74.9.4.0", {"center": v(20.6, -0.93) * mm, "radius": 1.25 * mm});
            skCircle(sketch, "E74.9.5.0", {"center": v(19.6, 3.97) * mm, "radius": 1.25 * mm});
            skCircle(sketch, "E74.9.6.0", {"center": v(18.6, 8.87) * mm, "radius": 1.25 * mm});
            skCircle(sketch, "E74.9.7.0", {"center": v(17.62, 13.77) * mm, "radius": 1.25 * mm});
            skCircle(sketch, "E74.9.8.0", {"center": v(16.62, 18.67) * mm, "radius": 1.25 * mm});
            skCircle(sketch, "E74.10.3.0", {"center": v(26.49, -4.84) * mm, "radius": 1.25 * mm});
            skCircle(sketch, "E74.10.4.0", {"center": v(25.5, 0.06) * mm, "radius": 1.25 * mm});
            skCircle(sketch, "E74.10.5.0", {"center": v(24.5, 4.96) * mm, "radius": 1.25 * mm});
            skCircle(sketch, "E74.10.6.0", {"center": v(23.5, 9.86) * mm, "radius": 1.25 * mm});
            skCircle(sketch, "E74.10.7.0", {"center": v(22.52, 14.76) * mm, "radius": 1.25 * mm});
            skLineSegment(sketch, "E74.direction1", {"start": v(56.32, -12.4) * mm, "end": v(60.3, -9.37) * mm, "construction": true});
            skLineSegment(sketch, "E74.direction2", {"start": v(56.32, -12.4) * mm, "end": v(53.29, -8.43) * mm, "construction": true});
            skLineSegment(sketch, "E75", {"start": v(-30.9, -6.15) * mm, "end": v(30.9, 6.15) * mm, "construction": true});
            skSolve(sketch);
        }
        {
            var Q0;
            Q0 = qSketchRegion(id + "F21", true);
            extrude(context, id + "F22", {"entities" : qUnion([Q0]), "operationType" : NewBodyOperationType.REMOVE, "oppositeDirection" : true, "depth" : 5 * mm, "offsetDistance" : 25 * mm});
        }
    });
